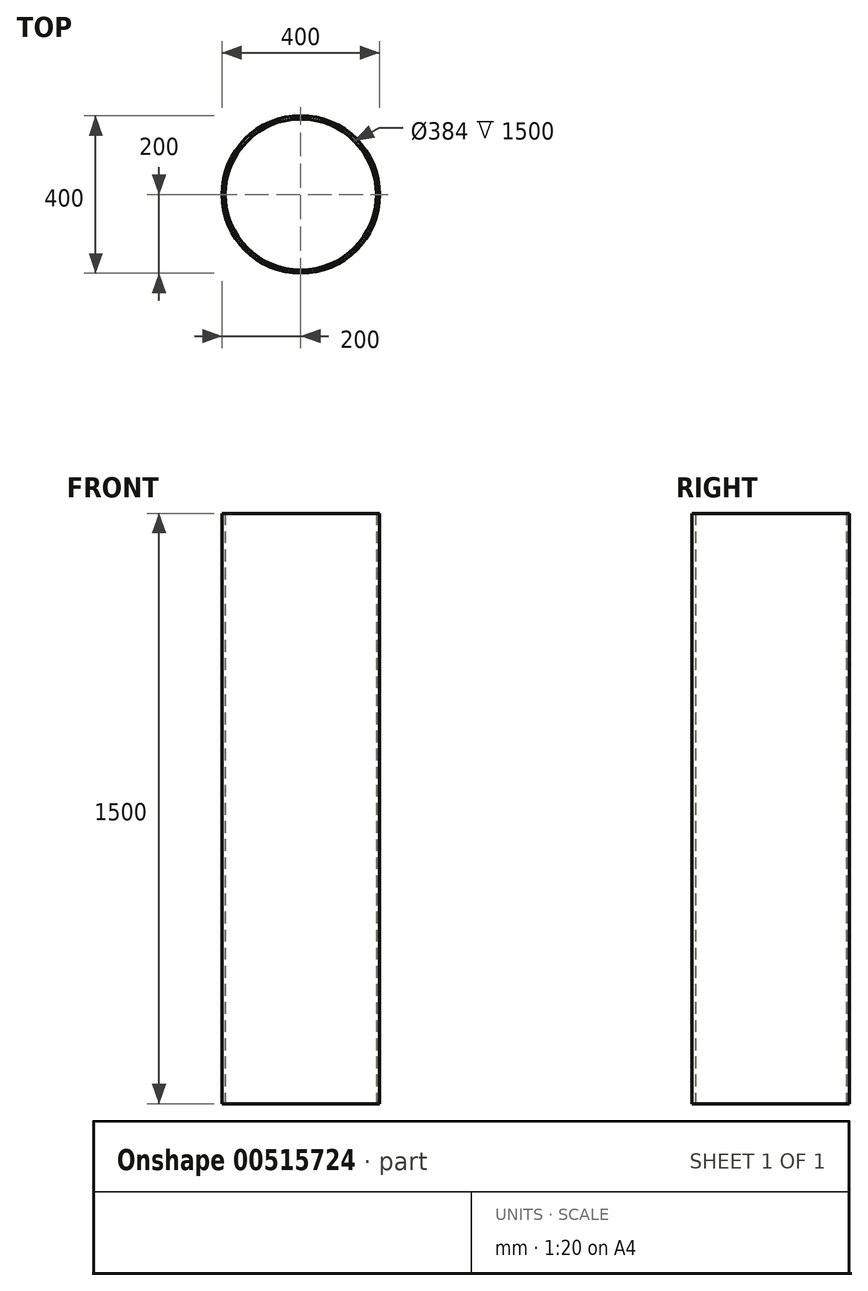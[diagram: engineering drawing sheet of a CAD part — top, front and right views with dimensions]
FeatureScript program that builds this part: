
annotation { "Feature Type Name" : "Feature", "Feature Type Description" : "" }
export const myFeature = defineFeature(function(context is Context, id is Id, definition is map)
    precondition{}
    {
        {
            var Q0;
            Q0=qCreatedBy(makeId("Top.planeOp"),FACE);
            var sketch = newSketch(context, id + "F0", { "sketchPlane" : qUnion([Q0])});
            skCircle(sketch, "E0", {"center": v(0, 0) * mm, "radius": 200 * mm});
            skCircle(sketch, "E1", {"center": v(0, 0) * mm, "radius": 192 * mm});
            skSolve(sketch);
        }
        {
            var Q0;
            Q0=makeQuery(id+"F0.imprint","IMPRINT",FACE,{"disambiguationData":[TD([[makeQuery(id+"F0.imprint","IMPRINT",EDGE,{"derivedFrom":sQuery(id+"F0.wireOp",EDGE,"E0")}),1.0]])]});
            extrude(context, id + "F1", {"entities" : qUnion([Q0]), "depth" : 1500 * mm, "offsetDistance" : 25 * mm});
        }
    });
